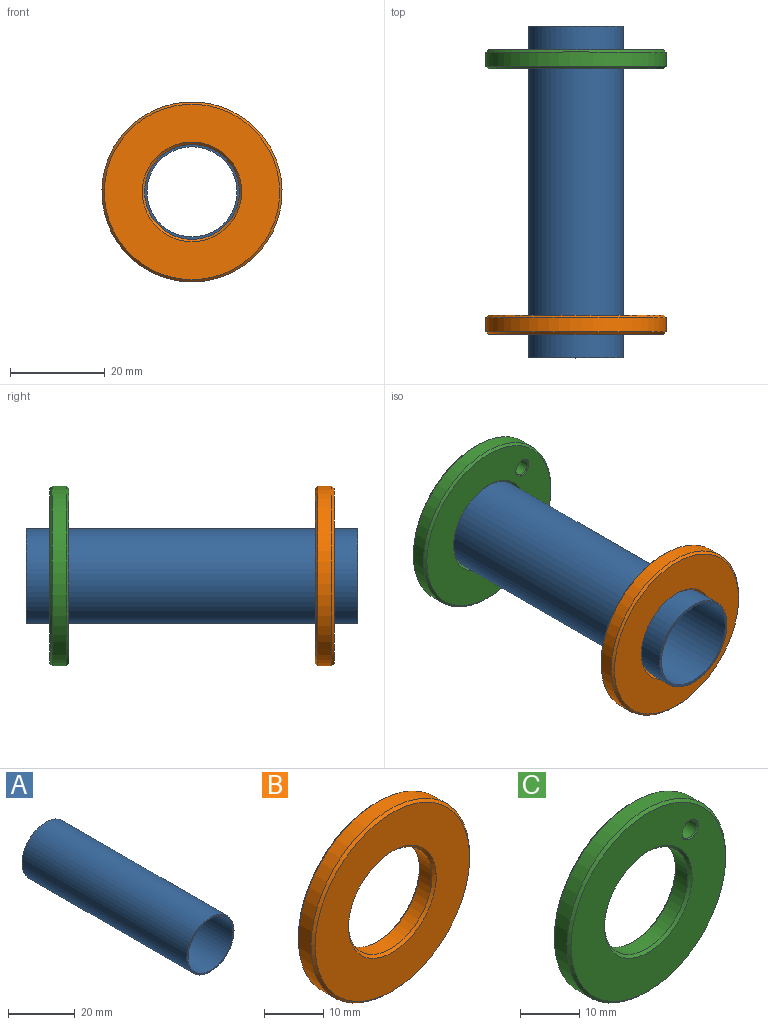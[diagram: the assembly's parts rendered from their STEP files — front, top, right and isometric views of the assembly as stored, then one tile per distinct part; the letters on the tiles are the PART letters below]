
ASSEMBLY  parts=3 mates=2
PART A: 4 faces, bbox 20x70x20 mm
  f0: cylinder r=9.5mm len=70mm, axis (0,-1,0), area 4178.3mm2, adj f2,f3
  f1: cylinder r=10mm len=70mm, axis (0,-1,0), area 4398.2mm2, adj f2,f3
  f2: plane 20x20mm, normal (0,1,0), area 30.6mm2, adj f0,f1
  f3: plane 20x20mm, normal (0,-1,0), area 30.6mm2, adj f0,f1
PART B: 8 faces, bbox 38x4x38 mm
  f0: cylinder r=10mm len=20mm, axis (0,1,0), area 188.5mm2, adj f4,f6
  f1: cylinder r=19mm len=38mm, axis (0,1,0), area 358.1mm2, adj f5,f7
  f2: plane 37x37mm, normal (0,-1,0), area 728.8mm2, adj f6,f7
  f3: plane 37x37mm, normal (0,1,0), area 728.8mm2, adj f4,f5
  f4: cone r=10.5mm half-angle=45deg, axis (0,1,0), area 45.5mm2, adj f0,f3
  f5: cone r=19mm half-angle=45deg, axis (0,-1,0), area 83.3mm2, adj f1,f3
  f6: cone r=10mm half-angle=45deg, axis (0,-1,0), area 45.5mm2, adj f0,f2
  f7: cone r=18.5mm half-angle=45deg, axis (0,1,0), area 83.3mm2, adj f1,f2
PART C: 11 faces, bbox 38x4x38 mm
  f0: cylinder r=1.75mm len=3.6mm, axis (0,1,0), area 39.6mm2, adj f9,f10
  f1: cylinder r=10mm len=20mm, axis (0,1,0), area 188.5mm2, adj f5,f6
  f2: cylinder r=19mm len=38mm, axis (0,1,0), area 358.1mm2, adj f7,f8
  f3: plane 37x37mm, normal (0,-1,0), area 716.9mm2, adj f6,f8,f10
  f4: plane 37x37mm, normal (0,1,0), area 716.9mm2, adj f5,f7,f9
  f5: cone r=10.5mm half-angle=45deg, axis (0,1,0), area 45.5mm2, adj f1,f4
  f6: cone r=10mm half-angle=45deg, axis (0,-1,0), area 45.5mm2, adj f1,f3
  f7: cone r=19mm half-angle=45deg, axis (0,-1,0), area 83.3mm2, adj f2,f4
  f8: cone r=18.5mm half-angle=45deg, axis (0,1,0), area 83.3mm2, adj f2,f3
  f9: cone r=1.95mm half-angle=45deg, axis (0,1,0), area 3.3mm2, adj f0,f4
  f10: cone r=1.75mm half-angle=45deg, axis (0,-1,0), area 3.3mm2, adj f0,f3
PLACE A t=(52.98,-20.58,10.39)mm
PLACE B t=(-11.08,-11.58,-35.49)mm
PLACE C t=(12.98,44.42,10.39)mm
MATE fastened B.f0 <-> A.f0  axis (0,-1,0) through (12.98,-15.58,10.39)mm
MATE fastened C.f1 <-> A.f1  axis (0,1,0) through (12.98,44.42,10.39)mm
